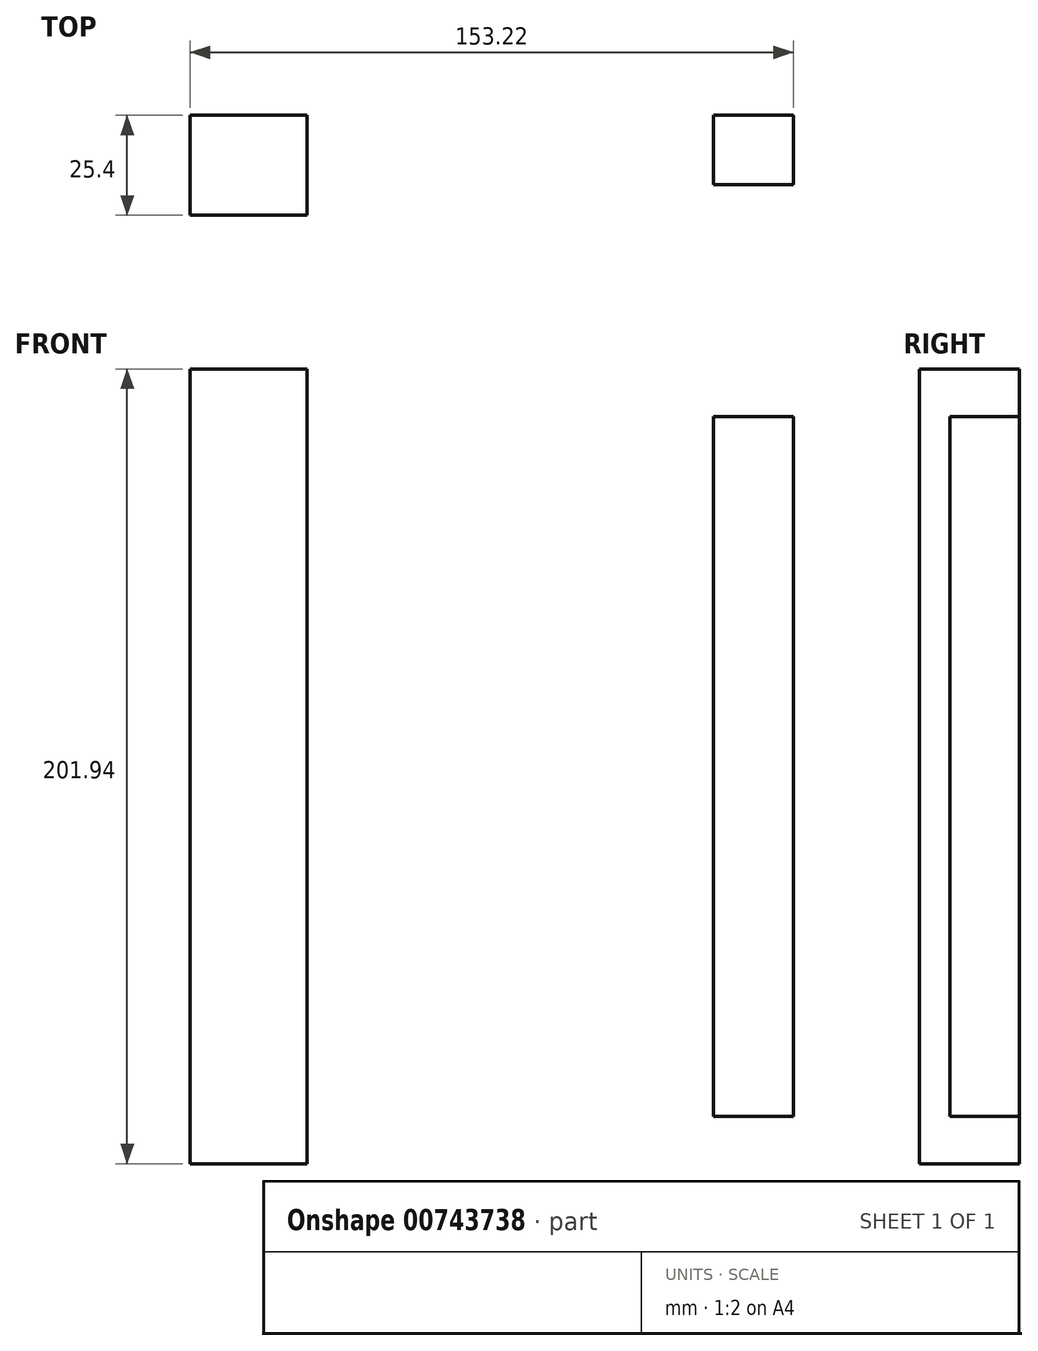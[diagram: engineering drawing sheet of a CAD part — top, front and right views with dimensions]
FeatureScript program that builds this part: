
annotation { "Feature Type Name" : "Feature", "Feature Type Description" : "" }
export const myFeature = defineFeature(function(context is Context, id is Id, definition is map)
    precondition{}
    {
        {
            var Q0;
            Q0=qCreatedBy(makeId("Front.planeOp"),FACE);
            var sketch = newSketch(context, id + "F0", { "sketchPlane" : qUnion([Q0])});
            skLineSegment(sketch, "E0.bottom", {"start": v(77.58, 88.9) * mm, "end": v(57.25, 88.9) * mm});
            skLineSegment(sketch, "E0.top", {"start": v(77.58, -88.9) * mm, "end": v(57.25, -88.9) * mm});
            skLineSegment(sketch, "E0.left", {"start": v(77.58, 88.9) * mm, "end": v(77.58, -88.9) * mm});
            skLineSegment(sketch, "E0.right", {"start": v(57.25, 88.9) * mm, "end": v(57.25, -88.9) * mm});
            skPoint(sketch, "E0.middle", {"position": v(67.42, 0) * mm});
            skLineSegment(sketch, "E1.bottom", {"start": v(-58.95, 88.9) * mm, "end": v(-76.22, 88.9) * mm});
            skLineSegment(sketch, "E1.top", {"start": v(-58.95, -88.9) * mm, "end": v(-76.22, -88.9) * mm});
            skLineSegment(sketch, "E1.left", {"start": v(-58.95, 88.9) * mm, "end": v(-58.95, -88.9) * mm});
            skLineSegment(sketch, "E1.right", {"start": v(-76.22, 88.9) * mm, "end": v(-76.22, -88.9) * mm});
            skPoint(sketch, "E1.middle", {"position": v(-67.59, 0) * mm});
            skSolve(sketch);
        }
        {
            var Q0;
            Q0=makeQuery(id+"F0.imprint","IMPRINT",FACE,{"disambiguationData":[TD([[makeQuery(id+"F0.imprint","IMPRINT",EDGE,{"derivedFrom":sQuery(id+"F0.wireOp",EDGE,"E0.bottom")}),1.0]])]});
            extrude(context, id + "F1", {"entities" : qUnion([Q0]), "depth" : 17.6 * mm, "offsetDistance" : 25.4 * mm});
        }
        {
            var Q0;
            Q0=qCreatedBy(makeId("Front.planeOp"),FACE);
            var sketch = newSketch(context, id + "F2", { "sketchPlane" : qUnion([Q0])});
            skLineSegment(sketch, "E2.bottom", {"start": v(-46, 100.97) * mm, "end": v(-75.64, 100.97) * mm});
            skLineSegment(sketch, "E2.top", {"start": v(-46, -100.97) * mm, "end": v(-75.64, -100.97) * mm});
            skLineSegment(sketch, "E2.left", {"start": v(-46, 100.97) * mm, "end": v(-46, -100.97) * mm});
            skLineSegment(sketch, "E2.right", {"start": v(-75.64, 100.97) * mm, "end": v(-75.64, -100.97) * mm});
            skPoint(sketch, "E2.middle", {"position": v(-60.82, 0) * mm});
            skSolve(sketch);
        }
        {
            var Q0;
            Q0=makeQuery(id+"F2.imprint","IMPRINT",FACE,{"disambiguationData":[TD([[makeQuery(id+"F2.imprint","IMPRINT",EDGE,{"derivedFrom":sQuery(id+"F2.wireOp",EDGE,"E2.bottom")}),1.0]])]});
            var sketch = newSketch(context, id + "F3", { "sketchPlane" : qUnion([Q0])});
            skSolve(sketch);
        }
        {
            var Q0;
            Q0=makeQuery(id+"F3.imprint","IMPRINT",FACE,{"disambiguationData":[TD([[makeQuery(id+"F3.imprint","IMPRINT",EDGE,{"derivedFrom":makeQuery(id+"F2.imprint","IMPRINT",EDGE,{"derivedFrom":sQuery(id+"F2.wireOp",EDGE,"E2.bottom")})}),1.0]])]});
            extrude(context, id + "F4", {"entities" : qUnion([Q0]), "depth" : 25.4 * mm, "offsetDistance" : 25.4 * mm});
        }
    });
